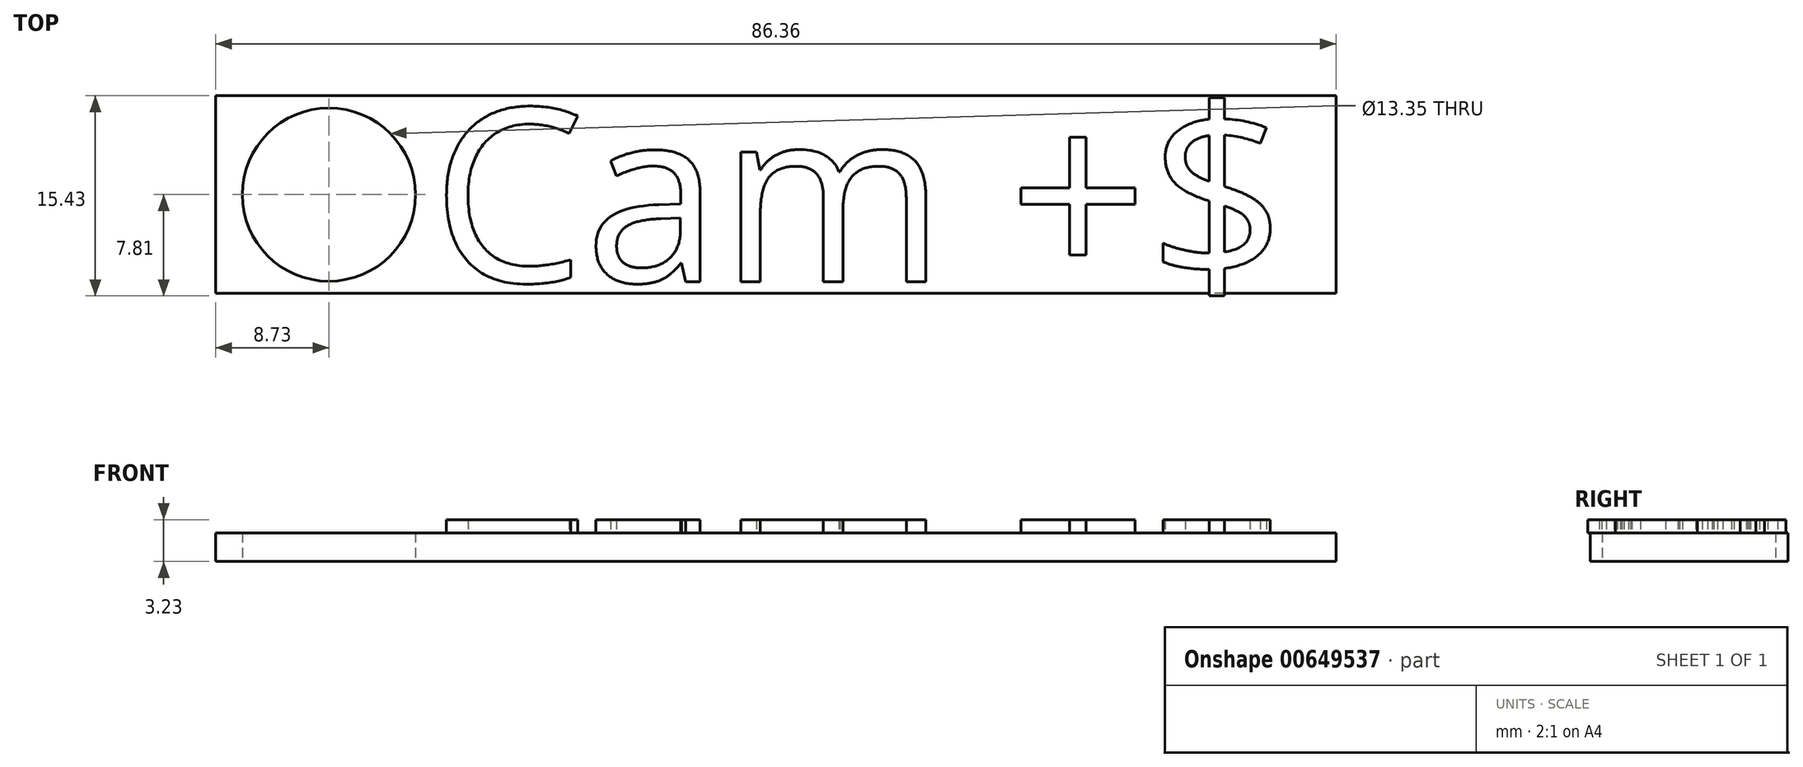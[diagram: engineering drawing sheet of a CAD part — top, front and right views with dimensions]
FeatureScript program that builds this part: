
annotation { "Feature Type Name" : "Feature", "Feature Type Description" : "" }
export const myFeature = defineFeature(function(context is Context, id is Id, definition is map)
    precondition{}
    {
        {
            var Q0;
            Q0=qCreatedBy(makeId("Top.planeOp"),FACE);
            var sketch = newSketch(context, id + "F0", { "sketchPlane" : qUnion([Q0])});
            skLineSegment(sketch, "E0.bottom", {"start": v(43.18, -7.62) * mm, "end": v(-43.18, -7.62) * mm});
            skLineSegment(sketch, "E0.top", {"start": v(43.18, 7.62) * mm, "end": v(-43.18, 7.62) * mm});
            skLineSegment(sketch, "E0.left", {"start": v(43.18, -7.62) * mm, "end": v(43.18, 7.62) * mm});
            skLineSegment(sketch, "E0.right", {"start": v(-43.18, -7.62) * mm, "end": v(-43.18, 7.62) * mm});
            skPoint(sketch, "E0.middle", {"position": v(0, 0) * mm});
            skCircle(sketch, "E1", {"center": v(-34.45, 0) * mm, "radius": 6.68 * mm});
            skSolve(sketch);
        }
        {
            var Q0;
            {var subQ0=sQuery(id+"F0.wireOp",EDGE,"E0.left");Q0=makeQuery(id+"F0.imprint","IMPRINT",FACE,{"disambiguationData":[TD([[makeQuery(id+"F0.imprint","IMPRINT",EDGE,{"derivedFrom":subQ0}),1.0]])]});}
            var Q1;
            {var subQ0=sQuery(id+"F0.wireOp",EDGE,"E0.right");Q1=makeQuery(id+"F0.imprint","IMPRINT",FACE,{"disambiguationData":[TD([[makeQuery(id+"F0.imprint","IMPRINT",EDGE,{"derivedFrom":subQ0}),-1.0]])]});}
            extrude(context, id + "F1", {"entities" : qUnion([Q0, Q1]), "depth" : 2.2 * mm, "offsetDistance" : 25.4 * mm});
        }
        {
            var Q0;
            Q0=makeQuery(id+"F1.opExtrude","CAP_FACE",FACE,{"disambiguationData":[OSD([sQuery(id+"F0.wireOp",EDGE,"E0.bottom"),sQuery(id+"F0.wireOp",EDGE,"E0.top"),sQuery(id+"F0.wireOp",EDGE,"E0.left"),sQuery(id+"F0.wireOp",EDGE,"E0.right"),sQuery(id+"F0.wireOp",EDGE,"E1")])],"isStart":false});
            var sketch = newSketch(context, id + "F2", { "sketchPlane" : qUnion([Q0])});
            skText(sketch, "E2", { "text": "Cam +$\n", "fontName": "OpenSans-Regular.ttf"});
            const initialGuessF2  = {"E2": [-0.02653, -0.00672, 1, 0, 0.01347]};
            skSetInitialGuess(sketch, initialGuessF2);
            skSolve(sketch);
        }
        {
            var Q0;
            Q0 = qSketchRegion(id + "F2", true);
            extrude(context, id + "F3", {"entities" : qUnion([Q0]), "operationType" : NewBodyOperationType.ADD, "depth" : 1.02 * mm, "offsetDistance" : 25.4 * mm});
        }
    });
